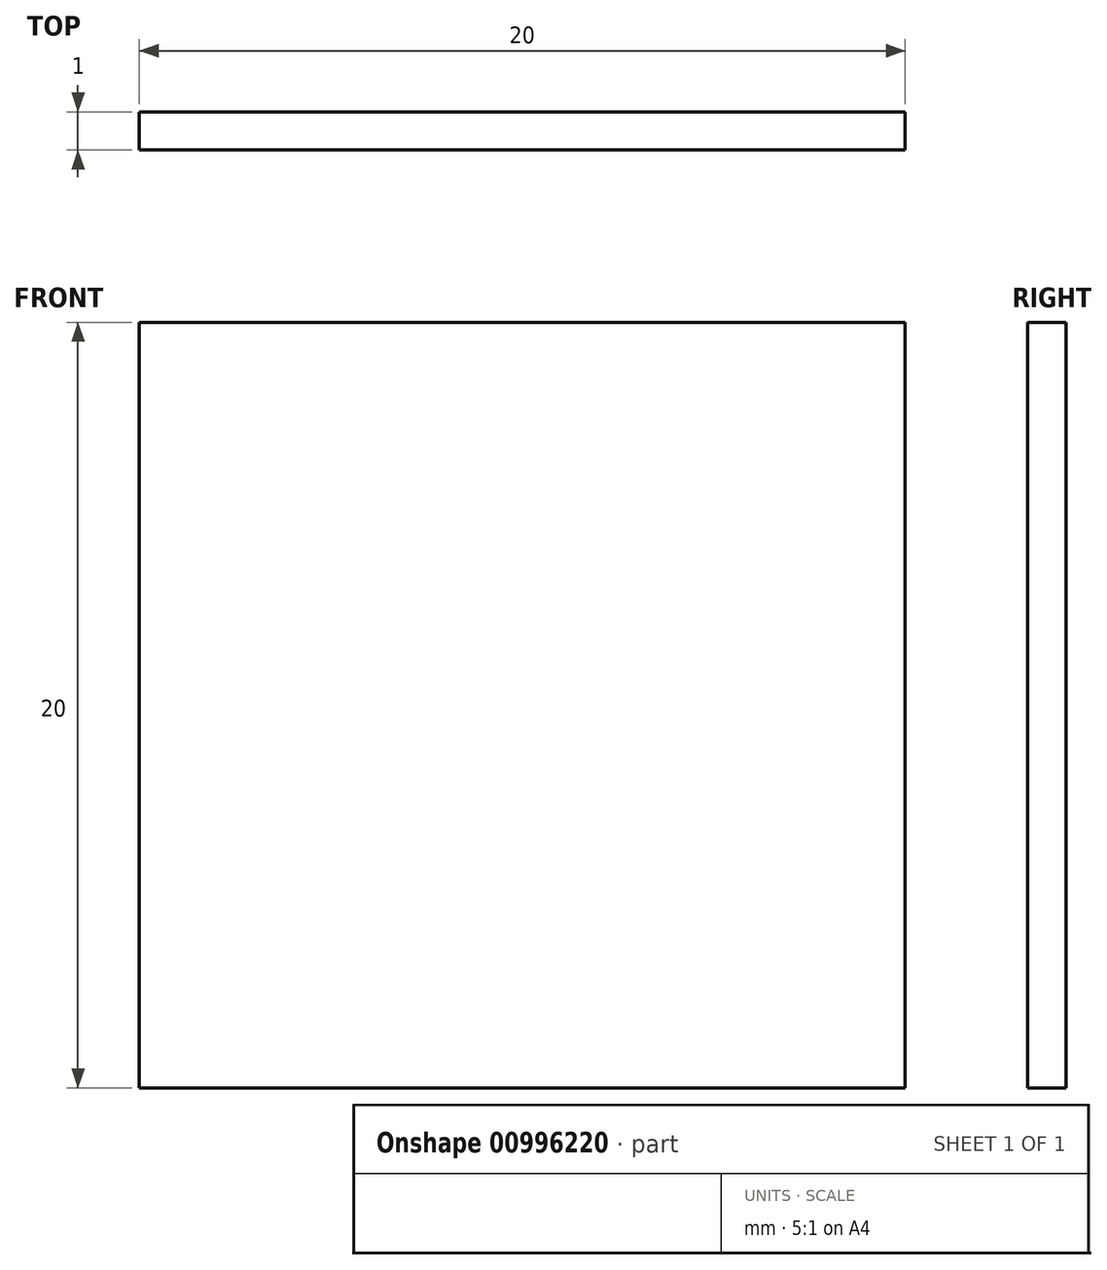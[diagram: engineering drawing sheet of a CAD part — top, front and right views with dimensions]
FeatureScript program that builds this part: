
annotation { "Feature Type Name" : "Feature", "Feature Type Description" : "" }
export const myFeature = defineFeature(function(context is Context, id is Id, definition is map)
    precondition{}
    {
        {
            var Q0;
            Q0=qCreatedBy(makeId("Front.planeOp"),FACE);
            var sketch = newSketch(context, id + "F0", { "sketchPlane" : qUnion([Q0])});
            skLineSegment(sketch, "E0.bottom", {"start": v(-10, 10) * mm, "end": v(10, 10) * mm});
            skLineSegment(sketch, "E0.top", {"start": v(-10, -10) * mm, "end": v(10, -10) * mm});
            skLineSegment(sketch, "E0.left", {"start": v(-10, 10) * mm, "end": v(-10, -10) * mm});
            skLineSegment(sketch, "E0.right", {"start": v(10, 10) * mm, "end": v(10, -10) * mm});
            skPoint(sketch, "E0.middle", {"position": v(0, 0) * mm});
            skSolve(sketch);
        }
        {
            var Q0;
            Q0=makeQuery(id+"F0.imprint","IMPRINT",FACE,{"disambiguationData":[TD([[makeQuery(id+"F0.imprint","IMPRINT",EDGE,{"derivedFrom":sQuery(id+"F0.wireOp",EDGE,"E0.bottom")}),-1.0]])]});
            extrude(context, id + "F1", {"entities" : qUnion([Q0]), "depth" : 1 * mm, "offsetDistance" : 25 * mm});
        }
    });
